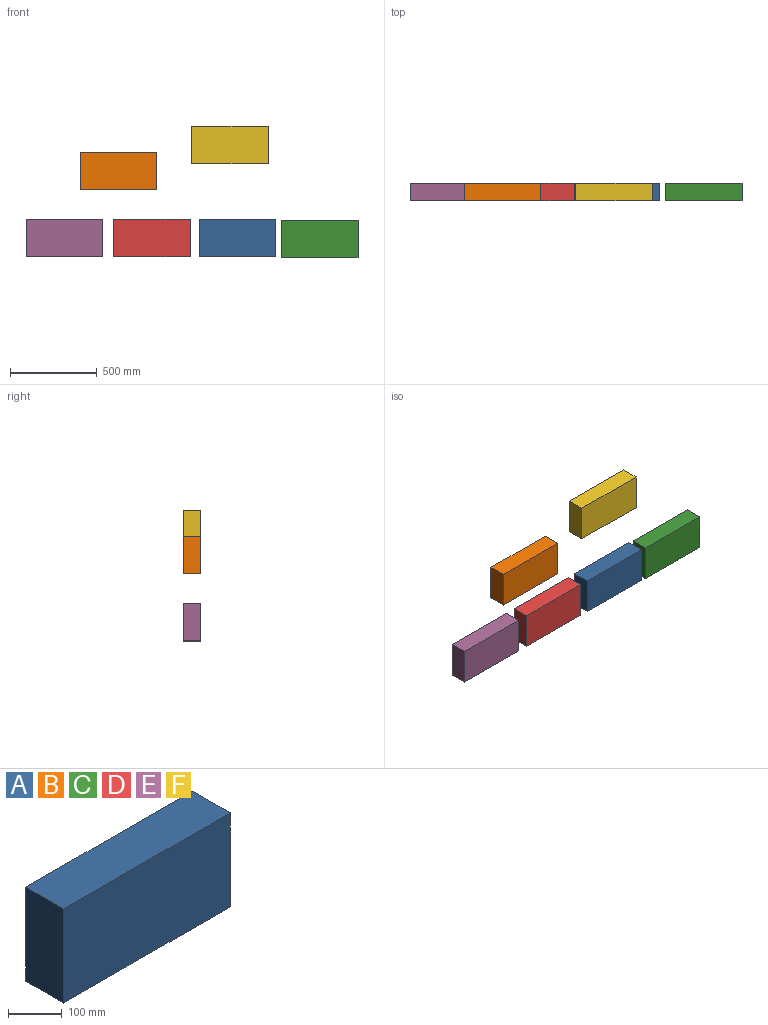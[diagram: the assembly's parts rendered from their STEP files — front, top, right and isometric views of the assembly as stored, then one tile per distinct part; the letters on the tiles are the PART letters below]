
ASSEMBLY  parts=6 mates=5
PART A: 6 faces, bbox 440x100x215 mm
  f0: plane 215x100mm, normal (1,0,0), area 21500mm2, adj f1,f3,f4,f5
  f1: plane 440x215mm, normal (0,1,0), area 94600mm2, adj f0,f2,f4,f5
  f2: plane 215x100mm, normal (-1,0,0), area 21500mm2, adj f1,f3,f4,f5
  f3: plane 440x215mm, normal (0,-1,0), area 94600mm2, adj f0,f2,f4,f5
  f4: plane 440x100mm, normal (0,0,1), area 44000mm2, adj f0,f1,f2,f3
  f5: plane 440x100mm, normal (0,0,-1), area 44000mm2, adj f0,f1,f2,f3
PART B: same geometry as A
PART C: same geometry as A
PART D: same geometry as A
PART E: same geometry as A
PART F: same geometry as A
PLACE A t=(995,0,0)mm
PLACE B t=(313,0,386)mm
PLACE C t=(1469.11,0,-5.8)mm
PLACE D t=(504,0,0)mm
PLACE E at identity fixed
PLACE F t=(953,0,533)mm
MATE planar B.f3 <-> C.f3  axis (0,-1,0) through (313,-50,493.5)mm
MATE planar D.f3 <-> A.f3  axis (0,-1,0) through (504,-50,107.5)mm
MATE planar B.f3 <-> F.f3  axis (0,-1,0) through (313,-50,493.5)mm
MATE planar A.f3 <-> B.f3  axis (0,-1,0) through (995,-50,107.5)mm
MATE planar E.f3 <-> D.f3  axis (0,-1,0) through (0,-50,107.5)mm
